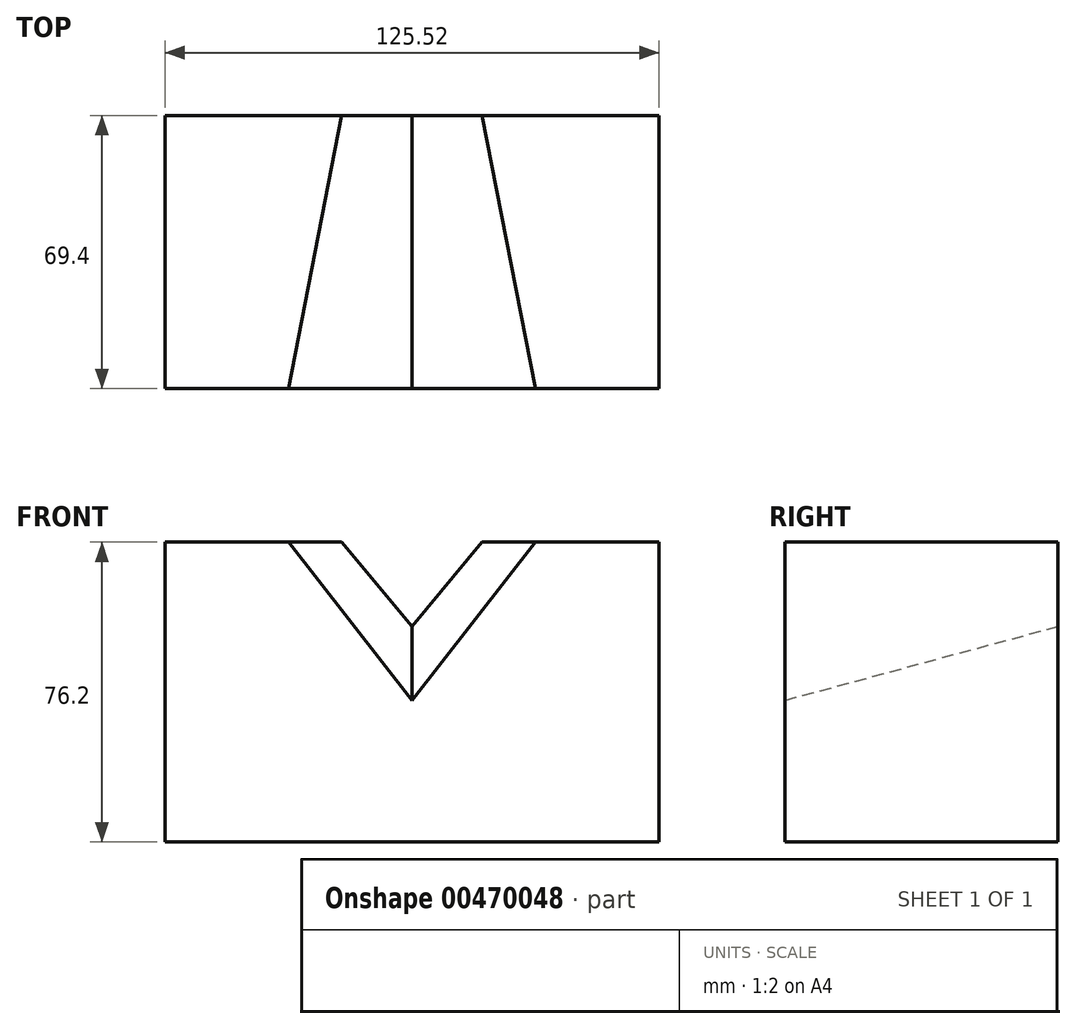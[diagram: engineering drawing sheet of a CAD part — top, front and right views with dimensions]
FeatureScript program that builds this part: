
annotation { "Feature Type Name" : "Feature", "Feature Type Description" : "" }
export const myFeature = defineFeature(function(context is Context, id is Id, definition is map)
    precondition{}
    {
        {
            var Q0;
            Q0=qCreatedBy(makeId("Top.planeOp"),FACE);
            var sketch = newSketch(context, id + "F0", { "sketchPlane" : qUnion([Q0])});
            skLineSegment(sketch, "E0.bottom", {"start": v(62.76, 34.7) * mm, "end": v(-62.76, 34.7) * mm});
            skLineSegment(sketch, "E0.top", {"start": v(62.76, -34.7) * mm, "end": v(-62.76, -34.7) * mm});
            skLineSegment(sketch, "E0.left", {"start": v(62.76, 34.7) * mm, "end": v(62.76, -34.7) * mm});
            skLineSegment(sketch, "E0.right", {"start": v(-62.76, 34.7) * mm, "end": v(-62.76, -34.7) * mm});
            skPoint(sketch, "E0.middle", {"position": v(0, 0) * mm});
            skSolve(sketch);
        }
        {
            var Q0;
            Q0 = qSketchRegion(id + "F0", true);
            extrude(context, id + "F1", {"entities" : qUnion([Q0]), "depth" : 76.2 * mm});
        }
        {
            var Q0;
            Q0=makeQuery(id+"F1.opExtrude","SWEPT_FACE",FACE,{"disambiguationData":[OSD([sQuery(id+"F0.wireOp",EDGE,"E0.top")])]});
            var sketch = newSketch(context, id + "F2", { "sketchPlane" : qUnion([Q0])});
            skLineSegment(sketch, "E1", {"start": v(0, 76.2) * mm, "end": v(0, 36.02) * mm, "construction": true});
            skPoint(sketch, "E1.endSnap0", {"position": v(0, 76.2) * mm});
            skLineSegment(sketch, "E2", {"start": v(0, 76.2) * mm, "end": v(-62.76, 76.2) * mm});
            skLineSegment(sketch, "E3", {"start": v(0, 76.2) * mm, "end": v(62.76, 76.2) * mm});
            skLineSegment(sketch, "E4", {"start": v(0, 36.02) * mm, "end": v(31.38, 76.2) * mm});
            skLineSegment(sketch, "E5", {"start": v(0, 36.02) * mm, "end": v(-31.38, 76.2) * mm});
            skSolve(sketch);
        }
        {
            var Q0;
            Q0=makeQuery(id+"F1.opExtrude","SWEPT_FACE",FACE,{"disambiguationData":[OSD([sQuery(id+"F0.wireOp",EDGE,"E0.bottom")])]});
            var sketch = newSketch(context, id + "F3", { "sketchPlane" : qUnion([Q0])});
            skLineSegment(sketch, "E6", {"start": v(0, 76.2) * mm, "end": v(0, 54.8) * mm, "construction": true});
            skPoint(sketch, "E6.endSnap0", {"position": v(0, 76.2) * mm});
            skLineSegment(sketch, "E7", {"start": v(-17.82, 76.2) * mm, "end": v(0, 76.2) * mm});
            skLineSegment(sketch, "E8", {"start": v(0, 76.2) * mm, "end": v(17.82, 76.2) * mm});
            skLineSegment(sketch, "E9", {"start": v(-17.82, 76.2) * mm, "end": v(0, 54.8) * mm});
            skLineSegment(sketch, "E10", {"start": v(17.82, 76.2) * mm, "end": v(0, 54.8) * mm});
            skSolve(sketch);
        }
        {
            var Q1;
            Q1 = qSketchRegion(id + "F2", true);
            var Q2;
            Q2 = qSketchRegion(id + "F3", true);
            var Q3;
            Q3 = qConstructionFilter(qBodyType(qCreatedBy(id + "F2" ,EDGE), BodyType.WIRE), ConstructionObject.NO);
            var Q4;
            Q4 = qConstructionFilter(qBodyType(qCreatedBy(id + "F3" ,EDGE), BodyType.WIRE), ConstructionObject.NO);
            loft(context, id + "F4", {"operationType" : NewBodyOperationType.REMOVE, "sheetProfilesArray" : [{ "sheetProfileEntities" : qUnion([Q1]) }, { "sheetProfileEntities" : qUnion([Q2]) }], "wireProfilesArray" : [{ "wireProfileEntities" : qUnion([Q3]) }, { "wireProfileEntities" : qUnion([Q4]) }]});
        }
    });
